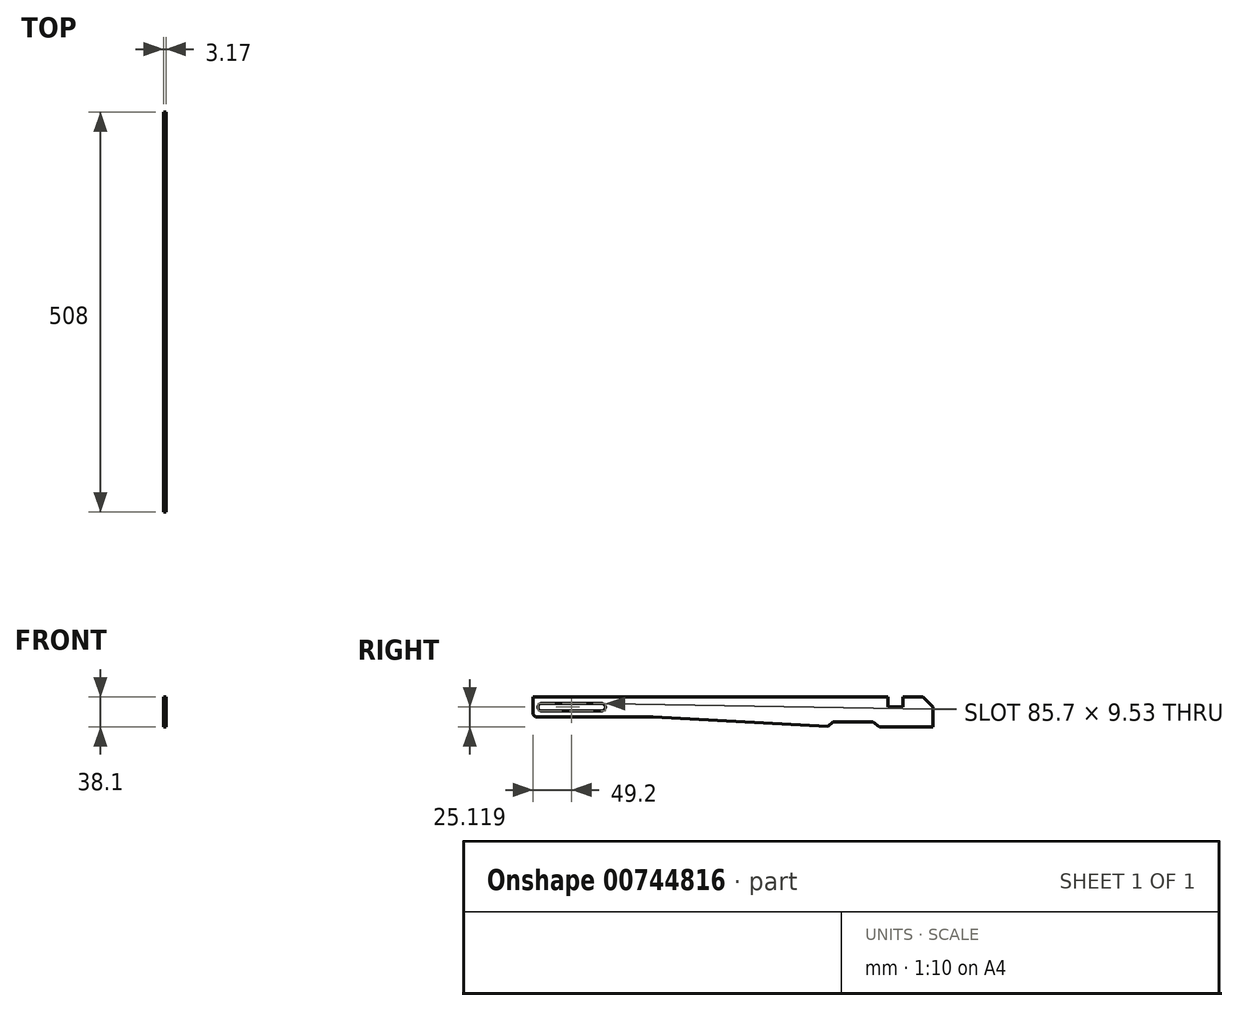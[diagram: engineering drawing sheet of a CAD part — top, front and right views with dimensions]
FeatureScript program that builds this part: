
annotation { "Feature Type Name" : "Feature", "Feature Type Description" : "" }
export const myFeature = defineFeature(function(context is Context, id is Id, definition is map)
    precondition{}
    {
        {
            var Q0;
            Q0=qCreatedBy(makeId("Right.planeOp"),FACE);
            var sketch = newSketch(context, id + "F0", { "sketchPlane" : qUnion([Q0])});
            skLineSegment(sketch, "E0", {"start": v(0, -27.77) * mm, "end": v(0, -53.17) * mm});
            skLineSegment(sketch, "E1", {"start": v(-38.1, -27.77) * mm, "end": v(-57.15, -27.77) * mm});
            skLineSegment(sketch, "E2", {"start": v(-57.15, -15.07) * mm, "end": v(-57.15, -27.77) * mm});
            skPoint(sketch, "E2.startSnap0", {"position": v(-38.1, -15.07) * mm});
            skLineSegment(sketch, "E3", {"start": v(-57.15, -15.07) * mm, "end": v(-209.55, -15.07) * mm});
            skLineSegment(sketch, "E4", {"start": v(-38.1, -15.07) * mm, "end": v(-12.7, -15.07) * mm});
            skLineSegment(sketch, "E5", {"start": v(-12.7, -15.07) * mm, "end": v(0, -27.77) * mm});
            skLineSegment(sketch, "E6", {"start": v(-38.1, -15.07) * mm, "end": v(-38.1, -27.77) * mm});
            skLineSegment(sketch, "E7", {"start": v(-213.71, -48.36) * mm, "end": v(-355.6, -40.47) * mm});
            skLineSegment(sketch, "E8", {"start": v(-127, -46.82) * mm, "end": v(-76.2, -46.82) * mm});
            skLineSegment(sketch, "E9", {"start": v(-67.67, -53.17) * mm, "end": v(-76.2, -46.82) * mm});
            skLineSegment(sketch, "E10", {"start": v(-127, -46.82) * mm, "end": v(-133.42, -52.82) * mm});
            skLineSegment(sketch, "E11", {"start": v(-133.42, -52.82) * mm, "end": v(-213.71, -48.36) * mm});
            skLineSegment(sketch, "E12", {"start": v(0, -53.17) * mm, "end": v(-67.67, -53.17) * mm});
            skLineSegment(sketch, "E13", {"start": v(-209.55, -15.07) * mm, "end": v(-508, -15.07) * mm});
            skLineSegment(sketch, "E14", {"start": v(-496.9, -23.29) * mm, "end": v(-420.7, -23.29) * mm});
            skArc(sketch, "E15", {"start": v(-496.9, -23.29) * mm, "mid": v(-501.65, -28.05) * mm, "end": v(-496.9, -32.81) * mm});
            skArc(sketch, "E16", {"start": v(-420.7, -32.81) * mm, "mid": v(-415.95, -28.05) * mm, "end": v(-420.7, -23.29) * mm});
            skLineSegment(sketch, "E17", {"start": v(-496.9, -32.81) * mm, "end": v(-420.7, -32.81) * mm});
            skLineSegment(sketch, "E18", {"start": v(-508, -34.12) * mm, "end": v(-508, -15.07) * mm});
            skLineSegment(sketch, "E19", {"start": v(-504.83, -40.47) * mm, "end": v(-508, -37.3) * mm});
            skLineSegment(sketch, "E20", {"start": v(-508, -37.3) * mm, "end": v(-508, -34.12) * mm});
            skLineSegment(sketch, "E21", {"start": v(-504.83, -40.47) * mm, "end": v(-355.6, -40.47) * mm});
            skSolve(sketch);
        }
        {
            var Q0;
            Q0=makeQuery(id+"F0.imprint","IMPRINT",FACE,{"disambiguationData":[TD([[makeQuery(id+"F0.imprint","IMPRINT",EDGE,{"derivedFrom":sQuery(id+"F0.wireOp",EDGE,"E0")}),-1.0]])]});
            extrude(context, id + "F1", {"entities" : qUnion([Q0]), "depth" : 3.17 * mm, "offsetDistance" : 25.4 * mm});
        }
    });
